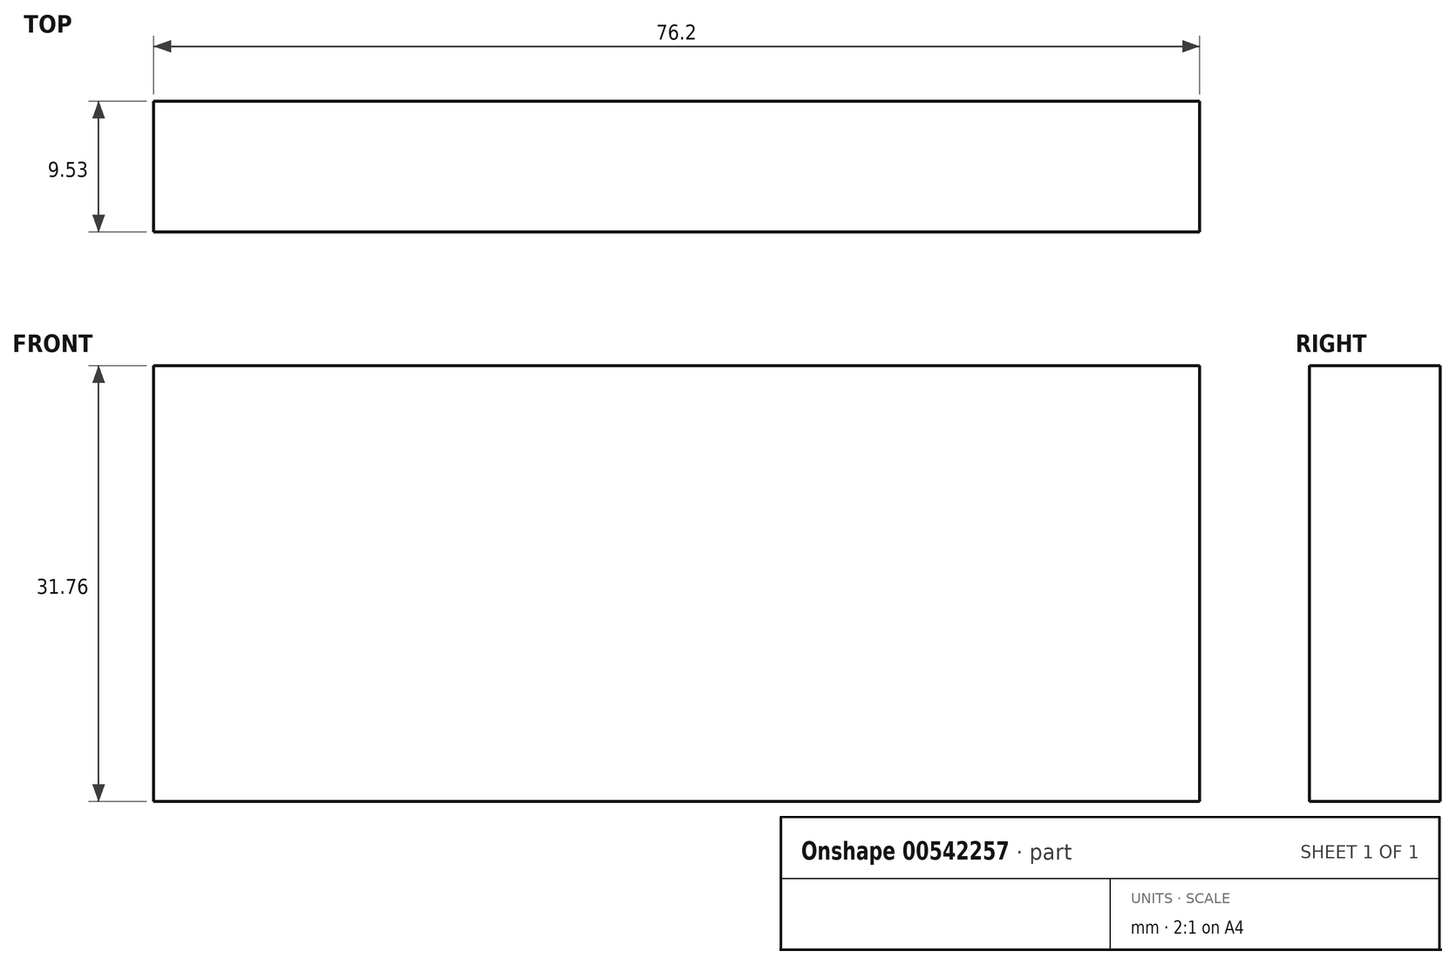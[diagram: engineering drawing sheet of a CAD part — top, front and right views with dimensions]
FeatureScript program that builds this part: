
annotation { "Feature Type Name" : "Feature", "Feature Type Description" : "" }
export const myFeature = defineFeature(function(context is Context, id is Id, definition is map)
    precondition{}
    {
        {
            var Q0;
            Q0=qCreatedBy(makeId("Front.planeOp"),FACE);
            var sketch = newSketch(context, id + "F0", { "sketchPlane" : qUnion([Q0])});
            skLineSegment(sketch, "E0.bottom", {"start": v(38.1, -15.87) * mm, "end": v(-38.1, -15.88) * mm});
            skLineSegment(sketch, "E0.top", {"start": v(38.1, 15.88) * mm, "end": v(-38.1, 15.88) * mm});
            skLineSegment(sketch, "E0.left", {"start": v(38.1, -15.87) * mm, "end": v(38.1, 15.88) * mm});
            skLineSegment(sketch, "E0.right", {"start": v(-38.1, -15.88) * mm, "end": v(-38.1, 15.88) * mm});
            skPoint(sketch, "E0.middle", {"position": v(0, 0) * mm});
            skSolve(sketch);
        }
        {
            var Q0;
            Q0 = qSketchRegion(id + "F0", true);
            extrude(context, id + "F1", {"entities" : qUnion([Q0]), "depth" : 9.52 * mm, "offsetDistance" : 25.4 * mm});
        }
    });
